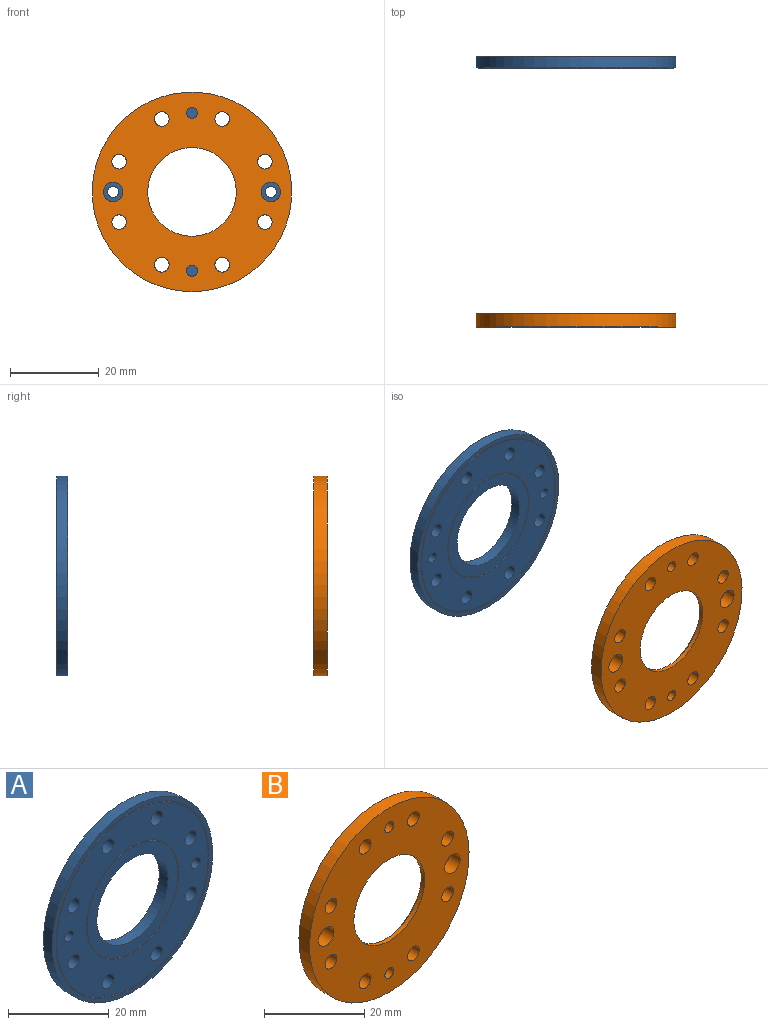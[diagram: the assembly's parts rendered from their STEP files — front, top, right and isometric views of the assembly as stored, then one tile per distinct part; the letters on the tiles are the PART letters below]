
ASSEMBLY  parts=2 mates=1
PART A: 30 faces, bbox 45x2.5x45 mm
  f0: plane 25.5x25.5mm, normal (0,1,0), area 196.5mm2, adj f4,f27
  f1: plane 42.5x42.5mm, normal (0,1,0), area 809.5mm2, adj f8,f9,f10,f11,f12,f13,f14,f15
  f2: plane 25.5x25.5mm, normal (0,-1,0), area 196.5mm2, adj f4,f21
  f3: plane 42.5x42.5mm, normal (0,-1,0), area 809.5mm2, adj f8,f9,f10,f11,f12,f13,f14,f15
  f4: cylinder r=10mm len=20mm, axis (0,1,0), area 157.1mm2, adj f0,f2
  f5: cylinder r=22.5mm len=45mm, axis (0,1,0), area 353.4mm2, adj f6,f7
  f6: plane 45x45mm, normal (0,-1,0), area 138.2mm2, adj f5,f19
  f7: plane 45x45mm, normal (0,1,0), area 138.2mm2, adj f5,f25
  f8: cylinder r=1.65mm len=3.3mm, axis (0,1,0), area 25.9mm2, adj f1,f3
  f9: cylinder r=1.65mm len=3.3mm, axis (0,1,0), area 25.9mm2, adj f1,f3
  f10: cylinder r=1.65mm len=3.3mm, axis (0,1,0), area 25.9mm2, adj f1,f3
  f11: cylinder r=1.65mm len=3.3mm, axis (0,1,0), area 25.9mm2, adj f1,f3
  f12: cylinder r=1.65mm len=3.3mm, axis (0,1,0), area 25.9mm2, adj f1,f3
  f13: cylinder r=1.65mm len=3.3mm, axis (0,1,0), area 25.9mm2, adj f1,f3
  f14: cylinder r=1.65mm len=3.3mm, axis (0,1,0), area 25.9mm2, adj f1,f3
  f15: cylinder r=1.65mm len=3.3mm, axis (0,1,0), area 25.9mm2, adj f1,f3
  f16: cylinder r=1.25mm len=2.5mm, axis (0,1,0), area 19.6mm2, adj f1,f3
  f17: cylinder r=1.25mm len=2.5mm, axis (0,1,0), area 19.6mm2, adj f1,f3
  f18: cylinder r=21.25mm len=42.5mm, axis (0,-1,0), area 66.8mm2, adj f3,f20
  f19: cylinder r=21.5mm len=43mm, axis (0,-1,0), area 67.5mm2, adj f6,f20
  f20: plane 43x43mm, normal (0,-1,0), area 33.6mm2, adj f18,f19
  f21: cylinder r=12.75mm len=25.5mm, axis (0,-1,0), area 40.1mm2, adj f2,f23
  f22: cylinder r=13mm len=26mm, axis (0,-1,0), area 40.8mm2, adj f3,f23
  f23: plane 26x26mm, normal (0,-1,0), area 20.2mm2, adj f21,f22
  f24: cylinder r=21.25mm len=42.5mm, axis (0,1,0), area 66.8mm2, adj f1,f26
  f25: cylinder r=21.5mm len=43mm, axis (0,1,0), area 67.5mm2, adj f7,f26
  f26: plane 43x43mm, normal (0,1,0), area 33.6mm2, adj f24,f25
  f27: cylinder r=12.75mm len=25.5mm, axis (0,1,0), area 40.1mm2, adj f0,f29
  f28: cylinder r=13mm len=26mm, axis (0,1,0), area 40.8mm2, adj f1,f29
  f29: plane 26x26mm, normal (0,1,0), area 20.2mm2, adj f27,f28
PART B: 18 faces, bbox 45x3x45 mm
  f0: plane 45x45mm, normal (0,1,0), area 983mm2, adj f2,f4,f5,f6,f7,f8,f9,f10
  f1: cylinder r=10mm len=20mm, axis (0,1,0), area 62.8mm2, adj f3,f15
  f2: cylinder r=22.5mm len=45mm, axis (0,1,0), area 424.1mm2, adj f0,f3
  f3: plane 45x45mm, normal (0,-1,0), area 1167.6mm2, adj f1,f2,f4,f5,f6,f7,f8,f9
  f4: cylinder r=1.65mm len=3.3mm, axis (0,1,0), area 31.1mm2, adj f0,f3
  f5: cylinder r=1.65mm len=3.3mm, axis (0,1,0), area 31.1mm2, adj f0,f3
  f6: cylinder r=1.65mm len=3.3mm, axis (0,1,0), area 31.1mm2, adj f0,f3
  f7: cylinder r=1.65mm len=3.3mm, axis (0,1,0), area 31.1mm2, adj f0,f3
  f8: cylinder r=1.65mm len=3.3mm, axis (0,1,0), area 31.1mm2, adj f0,f3
  f9: cylinder r=1.65mm len=3.3mm, axis (0,1,0), area 31.1mm2, adj f0,f3
  f10: cylinder r=1.65mm len=3.3mm, axis (0,1,0), area 31.1mm2, adj f0,f3
  f11: cylinder r=1.65mm len=3.3mm, axis (0,1,0), area 31.1mm2, adj f0,f3
  f12: cylinder r=2.2mm len=4.4mm, axis (0,1,0), area 41.5mm2, adj f0,f3
  f13: cylinder r=2.2mm len=4.4mm, axis (0,1,0), area 41.5mm2, adj f0,f3
  f14: cylinder r=12.6mm len=25.2mm, axis (0,1,0), area 158.3mm2, adj f0,f15
  f15: plane 25.2x25.2mm, normal (0,1,0), area 184.6mm2, adj f1,f14
  f16: cylinder r=1.25mm len=3mm, axis (0,1,0), area 23.6mm2, adj f0,f3
  f17: cylinder r=1.25mm len=3mm, axis (0,1,0), area 23.6mm2, adj f0,f3
PLACE A at identity fixed
PLACE B t=(0,-57.97,0)mm
MATE slider B.f12 <-> A.f16  axis (0,-1,0) through (-17.8,-60.97,0)mm
